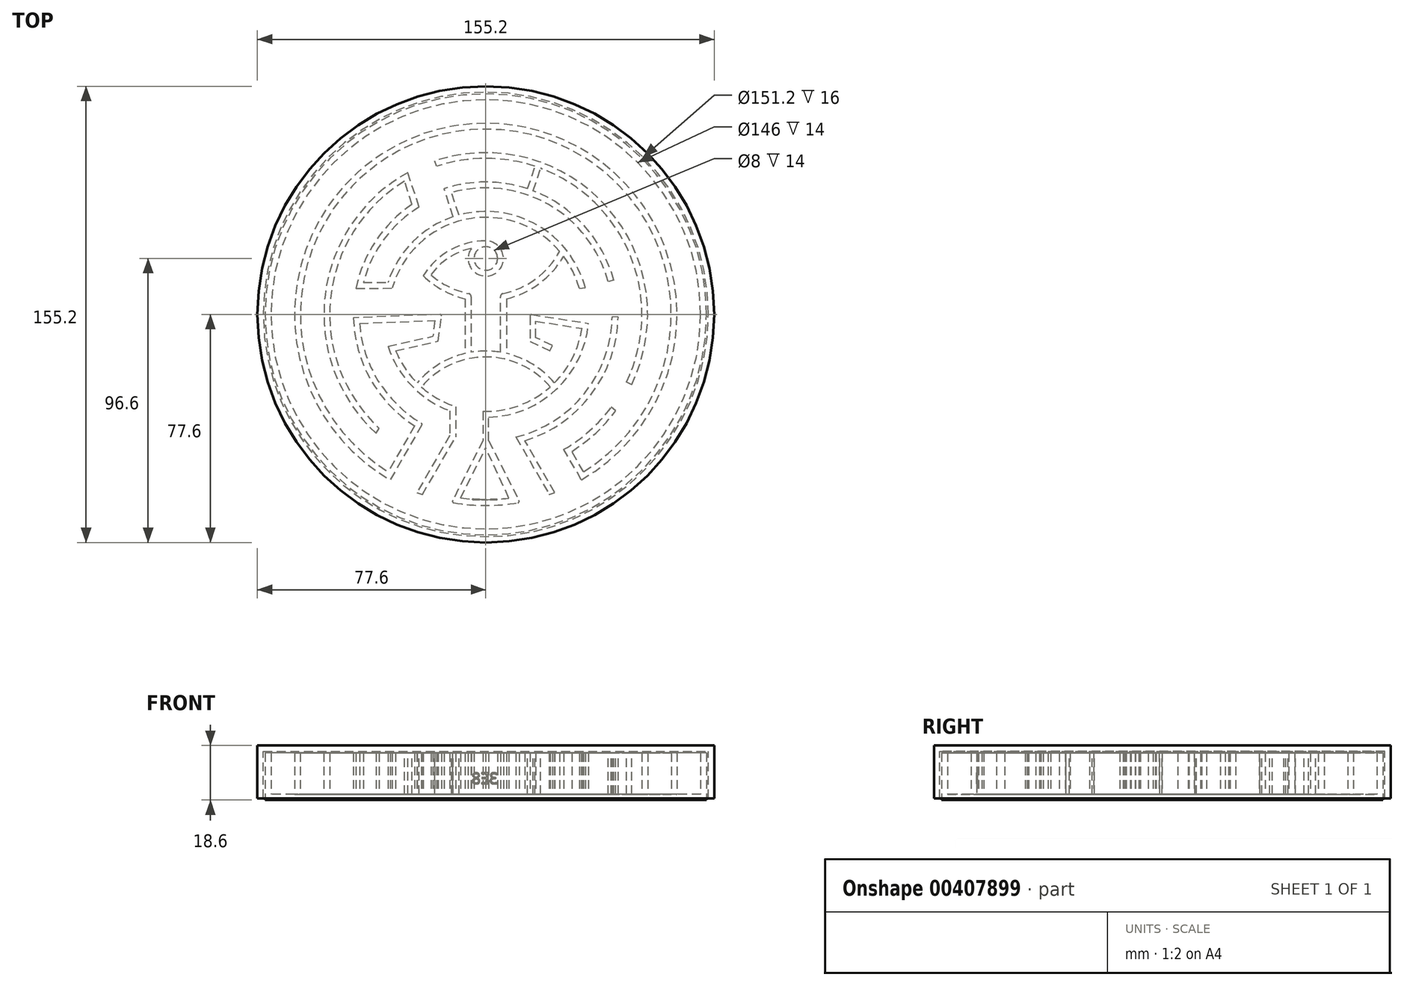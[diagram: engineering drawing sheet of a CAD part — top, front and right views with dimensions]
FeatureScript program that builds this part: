
annotation { "Feature Type Name" : "Feature", "Feature Type Description" : "" }
export const myFeature = defineFeature(function(context is Context, id is Id, definition is map)
    precondition{}
    {
        {
            assignVariable(context, id + "F0", {"name" : "OuterDiam", "anyValue" : 150});
        }
        {
            assignVariable(context, id + "F1", {"name" : "ChannelWidth", "anyValue" : getVariable(context, 'OuterDiam') / 15});
        }
        {
            assignVariable(context, id + "F2", {"name" : "WallThick", "anyValue" : 2});
        }
        {
            assignVariable(context, id + "F3", {"name" : "WallHeight", "anyValue" : getVariable(context, 'ChannelWidth') + getVariable(context, 'WallThick') * 2});
        }
        {
            var Q0;
            Q0=qCreatedBy(makeId("Top.planeOp"),FACE);
            var sketch = newSketch(context, id + "F4", { "sketchPlane" : qUnion([Q0])});
            skCircle(sketch, "E0", {"center": v(0, 0) * mm, "radius": 75 * mm});
            skSolve(sketch);
        }
        {
            var Q0;
            Q0=makeQuery(id+"F4.imprint","IMPRINT",FACE,{"disambiguationData":[TD([[makeQuery(id+"F4.imprint","IMPRINT",EDGE,{"derivedFrom":sQuery(id+"F4.wireOp",EDGE,"E0")}),1.0]])]});
            extrude(context, id + "F5", {"entities" : qUnion([Q0]), "depth" : (getVariable(context, 'WallThick')) * mm});
        }
        {
            var Q0;
            Q0=makeQuery(id+"F5.opExtrude","CAP_FACE",FACE,{"disambiguationData":[OSD([sQuery(id+"F4.wireOp",EDGE,"E0")])],"isStart":false});
            var sketch = newSketch(context, id + "F6", { "sketchPlane" : qUnion([Q0])});
            skCircle(sketch, "E1.0", {"center": v(0, 0) * mm, "radius": 75 * mm});
            skCircle(sketch, "E2.0", {"center": v(0, 0) * mm, "radius": 73 * mm});
            skCircle(sketch, "E3", {"center": v(0, 0) * mm, "radius": 65 * mm, "construction": true});
            skCircle(sketch, "E4", {"center": v(0, 0) * mm, "radius": 55 * mm, "construction": true});
            skCircle(sketch, "E5", {"center": v(0, 0) * mm, "radius": 45 * mm, "construction": true});
            skCircle(sketch, "E6", {"center": v(0, 0) * mm, "radius": 35 * mm, "construction": true});
            skCircle(sketch, "E7", {"center": v(0, 0) * mm, "radius": 5 * mm, "construction": true});
            skLineSegment(sketch, "E8", {"start": v(0, 35) * mm, "end": v(0, 45) * mm, "construction": true});
            skLineSegment(sketch, "E9", {"start": v(0, 45) * mm, "end": v(0, 55) * mm, "construction": true});
            skLineSegment(sketch, "E10", {"start": v(0, 55) * mm, "end": v(0, 65) * mm, "construction": true});
            skLineSegment(sketch, "E11", {"start": v(0, 65) * mm, "end": v(0, 75) * mm, "construction": true});
            skLineSegment(sketch, "E12", {"start": v(0, 0) * mm, "end": v(24.75, 24.75) * mm, "construction": true});
            skLineSegment(sketch, "E13", {"start": v(0, 0) * mm, "end": v(75, 0) * mm, "construction": true});
            skLineSegment(sketch, "E14.MirrorCS", {"start": v(0, 0) * mm, "end": v(24.75, -24.75) * mm, "construction": true});
            skLineSegment(sketch, "E15.MirrorCS", {"start": v(0, 0) * mm, "end": v(-16.5, 16.5) * mm, "construction": true});
            skLineSegment(sketch, "E16.MirrorCS", {"start": v(0, 0) * mm, "end": v(-23.33, -23.33) * mm, "construction": true});
            skCircle(sketch, "E17", {"center": v(0, 0) * mm, "radius": 10 * mm, "construction": true});
            skArc(sketch, "E18", {"start": v(-21.28, 13.13) * mm, "mid": v(-14.67, 8.24) * mm, "end": v(-7, 5.3) * mm});
            skArc(sketch, "E19", {"start": v(-18.67, 13.44) * mm, "mid": v(-12.27, 9.26) * mm, "end": v(-5, 6.92) * mm});
            skLineSegment(sketch, "E20", {"start": v(-7, 5.3) * mm, "end": v(-7, -13.3) * mm});
            skLineSegment(sketch, "E21", {"start": v(-5, 6.92) * mm, "end": v(-5, -12.9) * mm});
            skCircle(sketch, "E22.MirrorC", {"center": v(0, -43) * mm, "radius": 28.52 * mm, "construction": true});
            skArc(sketch, "E23", {"start": v(41.14, -50.32) * mm, "mid": v(-5.25, 64.79) * mm, "end": v(-32.5, -56.3) * mm});
            skArc(sketch, "E24", {"start": v(32.5, -56.3) * mm, "mid": v(0, 65) * mm, "end": v(-32.5, -56.3) * mm});
            skLineSegment(sketch, "E25", {"start": v(15.1, -7.04) * mm, "end": v(0, 0) * mm, "construction": true});
            skArc(sketch, "E26", {"start": v(-30.61, -12.33) * mm, "mid": v(-27.53, -18.2) * mm, "end": v(-23.33, -23.33) * mm});
            skArc(sketch, "E27", {"start": v(-7, -13.3) * mm, "mid": v(-15.98, -17) * mm, "end": v(-23.33, -23.33) * mm});
            skArc(sketch, "E28", {"start": v(-33.27, -10.87) * mm, "mid": v(-25.26, -24.22) * mm, "end": v(-12.25, -32.79) * mm});
            skLineSegment(sketch, "E29", {"start": v(-33.27, -10.87) * mm, "end": v(-17.96, -7.48) * mm});
            skArc(sketch, "E30", {"start": v(5, -12.9) * mm, "mid": v(0, -12.48) * mm, "end": v(-5, -12.9) * mm});
            skLineSegment(sketch, "E31", {"start": v(5, -12.9) * mm, "end": v(5, 6.92) * mm});
            skLineSegment(sketch, "E32", {"start": v(7, 5.3) * mm, "end": v(7, -13.3) * mm});
            skArc(sketch, "E33", {"start": v(5, 6.92) * mm, "mid": v(16.7, 11.88) * mm, "end": v(25.09, 21.44) * mm});
            skArc(sketch, "E34", {"start": v(33.22, -53.53) * mm, "mid": v(0, 63) * mm, "end": v(-33.22, -53.53) * mm});
            skArc(sketch, "E35", {"start": v(-44.99, -1.15) * mm, "mid": v(-39.18, -22.13) * mm, "end": v(-24.2, -37.93) * mm});
            skArc(sketch, "E36", {"start": v(-21.88, -24.7) * mm, "mid": v(-16.4, -28.63) * mm, "end": v(-10.25, -31.37) * mm});
            skArc(sketch, "E37", {"start": v(-42.9, -3.07) * mm, "mid": v(-36.45, -22.82) * mm, "end": v(-21.5, -37.24) * mm});
            skLineSegment(sketch, "E38", {"start": v(-17.28, -2.09) * mm, "end": v(-17.96, -7.48) * mm});
            skLineSegment(sketch, "E39", {"start": v(-30.61, -12.33) * mm, "end": v(-16.15, -9.13) * mm});
            skLineSegment(sketch, "E40", {"start": v(-16.15, -9.13) * mm, "end": v(-15, 0) * mm});
            skLineSegment(sketch, "E41", {"start": v(-10.25, -31.37) * mm, "end": v(-10.25, -41.76) * mm});
            skLineSegment(sketch, "E42", {"start": v(-12.25, -32.79) * mm, "end": v(-12.25, -41.22) * mm});
            skLineSegment(sketch, "E43", {"start": v(0, -43) * mm, "end": v(0, -45) * mm, "construction": true});
            skLineSegment(sketch, "E44", {"start": v(-1, -32.98) * mm, "end": v(-1, -42.99) * mm});
            skArc(sketch, "E45", {"start": v(-1, -32.98) * mm, "mid": v(11.23, -31.03) * mm, "end": v(21.88, -24.7) * mm});
            skLineSegment(sketch, "E46", {"start": v(1, -42.99) * mm, "end": v(1, -34.99) * mm});
            skLineSegment(sketch, "E47", {"start": v(15, 0) * mm, "end": v(15, -9.2) * mm});
            skLineSegment(sketch, "E48", {"start": v(21.81, -12.38) * mm, "end": v(22.66, -10.57) * mm});
            skLineSegment(sketch, "E49", {"start": v(22.66, -10.57) * mm, "end": v(17, -7.93) * mm});
            skLineSegment(sketch, "E50", {"start": v(17, -7.93) * mm, "end": v(17, -2.33) * mm});
            skArc(sketch, "E51", {"start": v(23.33, -23.33) * mm, "mid": v(15.98, -17) * mm, "end": v(7, -13.3) * mm});
            skArc(sketch, "E52", {"start": v(21.88, -24.7) * mm, "mid": v(0, -14.48) * mm, "end": v(-21.88, -24.7) * mm});
            skLineSegment(sketch, "E53", {"start": v(15, -9.2) * mm, "end": v(21.81, -12.38) * mm});
            skLineSegment(sketch, "E54", {"start": v(15, 0) * mm, "end": v(34.86, -3.07) * mm});
            skLineSegment(sketch, "E55", {"start": v(17, -2.33) * mm, "end": v(32.66, -4.75) * mm});
            skArc(sketch, "E56", {"start": v(23.33, -23.33) * mm, "mid": v(29.5, -14.8) * mm, "end": v(32.66, -4.75) * mm});
            skArc(sketch, "E57", {"start": v(1, -34.99) * mm, "mid": v(24, -25.47) * mm, "end": v(34.86, -3.07) * mm});
            skArc(sketch, "E58", {"start": v(31.8, 8.81) * mm, "mid": v(0.05, 33) * mm, "end": v(-31.77, 8.91) * mm});
            skArc(sketch, "E59", {"start": v(33.8, 9.07) * mm, "mid": v(0.96, 34.99) * mm, "end": v(-33.26, 10.9) * mm});
            skLineSegment(sketch, "E60", {"start": v(31.8, 8.81) * mm, "end": v(33.8, 9.07) * mm});
            skLineSegment(sketch, "E61", {"start": v(-32.5, -56.3) * mm, "end": v(0, 0) * mm, "construction": true});
            skLineSegment(sketch, "E62", {"start": v(-21.5, -37.24) * mm, "end": v(-32.5, -56.3) * mm});
            skLineSegment(sketch, "E63", {"start": v(-24.2, -37.93) * mm, "end": v(-33.22, -53.53) * mm});
            skArc(sketch, "E64", {"start": v(29.21, -46.6) * mm, "mid": v(5.04, 54.77) * mm, "end": v(-37.23, -40.48) * mm});
            skArc(sketch, "E65", {"start": v(26.52, -45.94) * mm, "mid": v(6.04, 52.7) * mm, "end": v(-36.23, -38.75) * mm});
            skLineSegment(sketch, "E66", {"start": v(-37.23, -40.48) * mm, "end": v(-36.23, -38.75) * mm});
            skLineSegment(sketch, "E67", {"start": v(0, 0) * mm, "end": v(32.5, -56.3) * mm, "construction": true});
            skLineSegment(sketch, "E68", {"start": v(32.5, -56.3) * mm, "end": v(26.52, -45.94) * mm});
            skLineSegment(sketch, "E69", {"start": v(33.22, -53.53) * mm, "end": v(29.21, -46.6) * mm});
            skLineSegment(sketch, "E70", {"start": v(-12.25, -41.22) * mm, "end": v(-23.45, -60.62) * mm});
            skLineSegment(sketch, "E71", {"start": v(-23.45, -60.62) * mm, "end": v(-21.58, -61.31) * mm});
            skLineSegment(sketch, "E72", {"start": v(-21.58, -61.31) * mm, "end": v(-10.25, -41.76) * mm});
            skLineSegment(sketch, "E73", {"start": v(-1, -42.99) * mm, "end": v(-11.58, -63.96) * mm});
            skArc(sketch, "E74", {"start": v(13.28, -43) * mm, "mid": v(30.17, 33.4) * mm, "end": v(-44.12, 8.85) * mm});
            skArc(sketch, "E75", {"start": v(10.28, -41.75) * mm, "mid": v(30.62, 30.2) * mm, "end": v(-41.6, 10.87) * mm});
            skLineSegment(sketch, "E76", {"start": v(-41.6, 10.87) * mm, "end": v(-33.26, 10.9) * mm});
            skLineSegment(sketch, "E77", {"start": v(-44.12, 8.85) * mm, "end": v(-31.77, 8.91) * mm});
            skLineSegment(sketch, "E78", {"start": v(10.28, -41.75) * mm, "end": v(21.58, -61.31) * mm});
            skLineSegment(sketch, "E79", {"start": v(21.58, -61.31) * mm, "end": v(23.45, -60.62) * mm});
            skLineSegment(sketch, "E80", {"start": v(23.45, -60.62) * mm, "end": v(13.28, -43) * mm});
            skArc(sketch, "E81", {"start": v(-21.5, -37.24) * mm, "mid": v(-6.05, -42.57) * mm, "end": v(10.28, -41.75) * mm, "construction": true});
            skLineSegment(sketch, "E82", {"start": v(1, -42.99) * mm, "end": v(11.58, -63.96) * mm});
            skArc(sketch, "E83", {"start": v(-11.58, -63.96) * mm, "mid": v(0, -65) * mm, "end": v(11.58, -63.96) * mm});
            skArc(sketch, "E84", {"start": v(-8.56, -62.42) * mm, "mid": v(-0.35, -63) * mm, "end": v(7.87, -62.5) * mm});
            skLineSegment(sketch, "E85", {"start": v(-8.56, -62.42) * mm, "end": v(0, -45.45) * mm});
            skLineSegment(sketch, "E86", {"start": v(7.87, -62.5) * mm, "end": v(0, -45.45) * mm});
            skLineSegment(sketch, "E87", {"start": v(0, 5) * mm, "end": v(0, 15) * mm, "construction": true});
            skLineSegment(sketch, "E88", {"start": v(0, 15) * mm, "end": v(0, 25) * mm, "construction": true});
            skLineSegment(sketch, "E89", {"start": v(0, 25) * mm, "end": v(0, 35) * mm, "construction": true});
            skCircle(sketch, "E90", {"center": v(0, 0) * mm, "radius": 25 * mm, "construction": true});
            skArc(sketch, "E91", {"start": v(0, 25) * mm, "mid": v(-12.18, 21.83) * mm, "end": v(-21.28, 13.13) * mm});
            skArc(sketch, "E92", {"start": v(-4.9, 22.47) * mm, "mid": v(-12.62, 19.23) * mm, "end": v(-18.67, 13.44) * mm});
            skArc(sketch, "E93", {"start": v(-4.9, 22.47) * mm, "mid": v(2.75, 13.67) * mm, "end": v(0, 25) * mm});
            skCircle(sketch, "E94", {"center": v(0, 19) * mm, "radius": 4 * mm});
            skLineSegment(sketch, "E95", {"start": v(4, 19) * mm, "end": v(6, 19) * mm, "construction": true});
            skLineSegment(sketch, "E96", {"start": v(5, 19) * mm, "end": v(5, 6.92) * mm, "construction": true});
            skArc(sketch, "E97", {"start": v(7, 5.3) * mm, "mid": v(18.21, 10.51) * mm, "end": v(26.43, 19.75) * mm});
            skLineSegment(sketch, "E98", {"start": v(-42.9, -3.07) * mm, "end": v(-17.28, -2.09) * mm});
            skLineSegment(sketch, "E99", {"start": v(-15, 0) * mm, "end": v(-44.99, -1.15) * mm});
            skLineSegment(sketch, "E100", {"start": v(-15, 0) * mm, "end": v(15, 0) * mm, "construction": true});
            skLineSegment(sketch, "E101", {"start": v(0, 5) * mm, "end": v(0, 0) * mm, "construction": true});
            skSolve(sketch);
        }
        {
            var Q0;
            Q0=makeQuery(id+"F6.imprint","IMPRINT",FACE,{"disambiguationData":[TD([[makeQuery(id+"F6.imprint","IMPRINT",EDGE,{"derivedFrom":sQuery(id+"F6.wireOp",EDGE,"E1.0")}),1.0]])]});
            var Q1;
            Q1=makeQuery(id+"F6.imprint","IMPRINT",FACE,{"disambiguationData":[TD([[makeQuery(id+"F6.imprint","IMPRINT",EDGE,{"derivedFrom":sQuery(id+"F6.wireOp",EDGE,"E18")}),1.0]])]});
            var Q2;
            Q2=makeQuery(id+"F6.imprint","IMPRINT",FACE,{"disambiguationData":[TD([[makeQuery(id+"F6.imprint","IMPRINT",EDGE,{"derivedFrom":sQuery(id+"F6.wireOp",EDGE,"E59")}),1.0]])]});
            extrude(context, id + "F7", {"entities" : qUnion([Q0, Q1, Q2]), "operationType" : NewBodyOperationType.ADD, "depth" : (getVariable(context, 'WallHeight')) * mm});
        }
        {
            var Q0;
            Q0=makeQuery(id+"F7.opExtrude","CAP_FACE",FACE,{"disambiguationData":[OSD([sQuery(id+"F6.wireOp",EDGE,"TA0vL4iM-hI7p-0iIZ-EZH9-pWyA7mMgioLP"),sQuery(id+"F6.wireOp",EDGE,"eVbhxhPi-amxz-cSnw-BDjh-pJRtyq95g7uy"),sQuery(id+"F6.wireOp",EDGE,"3bY1lwaK-FQGh-TaTl-XcqF-0j4MG99JuUr8"),sQuery(id+"F6.wireOp",EDGE,"r5nHWF7N-89Eq-ztux-vKRJ-OAizSOWOkK4G"),sQuery(id+"F6.wireOp",EDGE,"vSMcaTa0-RPhz-RhFH-5GNV-4O4aKqDjyfSq"),sQuery(id+"F6.wireOp",EDGE,"E18"),sQuery(id+"F6.wireOp",EDGE,"E19"),sQuery(id+"F6.wireOp",EDGE,"c2zhrxeP-xiZB-5hTI-5geB-tCFFj0RtpMOh"),sQuery(id+"F6.wireOp",EDGE,"E20"),sQuery(id+"F6.wireOp",EDGE,"E21"),sQuery(id+"F6.wireOp",EDGE,"E24"),sQuery(id+"F6.wireOp",EDGE,"E26"),sQuery(id+"F6.wireOp",EDGE,"E27"),sQuery(id+"F6.wireOp",EDGE,"E28"),sQuery(id+"F6.wireOp",EDGE,"E29"),sQuery(id+"F6.wireOp",EDGE,"E30"),sQuery(id+"F6.wireOp",EDGE,"E31"),sQuery(id+"F6.wireOp",EDGE,"E32"),sQuery(id+"F6.wireOp",EDGE,"E33"),sQuery(id+"F6.wireOp",EDGE,"w3oIxx7T-loaL-NBMZ-wnJf-bmkmqDUJZ4SM"),sQuery(id+"F6.wireOp",EDGE,"E34"),sQuery(id+"F6.wireOp",EDGE,"E35"),sQuery(id+"F6.wireOp",EDGE,"QwFV82SE-m3OC-BQkn-0jzC-JCZTuH3WHQPn"),sQuery(id+"F6.wireOp",EDGE,"E36"),sQuery(id+"F6.wireOp",EDGE,"E37"),sQuery(id+"F6.wireOp",EDGE,"ANerLEZW-9gPT-yuOP-Ji07-4zPnV21XRaUt"),sQuery(id+"F6.wireOp",EDGE,"E38"),sQuery(id+"F6.wireOp",EDGE,"E39"),sQuery(id+"F6.wireOp",EDGE,"E40"),sQuery(id+"F6.wireOp",EDGE,"E41"),sQuery(id+"F6.wireOp",EDGE,"E42"),sQuery(id+"F6.wireOp",EDGE,"E44"),sQuery(id+"F6.wireOp",EDGE,"E45"),sQuery(id+"F6.wireOp",EDGE,"E46"),sQuery(id+"F6.wireOp",EDGE,"E47"),sQuery(id+"F6.wireOp",EDGE,"E48"),sQuery(id+"F6.wireOp",EDGE,"E49"),sQuery(id+"F6.wireOp",EDGE,"E50"),sQuery(id+"F6.wireOp",EDGE,"E51"),sQuery(id+"F6.wireOp",EDGE,"E52"),sQuery(id+"F6.wireOp",EDGE,"E53"),sQuery(id+"F6.wireOp",EDGE,"E54"),sQuery(id+"F6.wireOp",EDGE,"E55"),sQuery(id+"F6.wireOp",EDGE,"E56"),sQuery(id+"F6.wireOp",EDGE,"E57"),sQuery(id+"F6.wireOp",EDGE,"E58"),sQuery(id+"F6.wireOp",EDGE,"E59"),sQuery(id+"F6.wireOp",EDGE,"E60"),sQuery(id+"F6.wireOp",EDGE,"E62"),sQuery(id+"F6.wireOp",EDGE,"E63"),sQuery(id+"F6.wireOp",EDGE,"E64"),sQuery(id+"F6.wireOp",EDGE,"E65"),sQuery(id+"F6.wireOp",EDGE,"E66"),sQuery(id+"F6.wireOp",EDGE,"E68"),sQuery(id+"F6.wireOp",EDGE,"E69"),sQuery(id+"F6.wireOp",EDGE,"E70"),sQuery(id+"F6.wireOp",EDGE,"E71"),sQuery(id+"F6.wireOp",EDGE,"E72"),sQuery(id+"F6.wireOp",EDGE,"E73"),sQuery(id+"F6.wireOp",EDGE,"E74"),sQuery(id+"F6.wireOp",EDGE,"E75"),sQuery(id+"F6.wireOp",EDGE,"E76"),sQuery(id+"F6.wireOp",EDGE,"E77"),sQuery(id+"F6.wireOp",EDGE,"E78"),sQuery(id+"F6.wireOp",EDGE,"E79"),sQuery(id+"F6.wireOp",EDGE,"E80"),sQuery(id+"F6.wireOp",EDGE,"E82"),sQuery(id+"F6.wireOp",EDGE,"E83"),sQuery(id+"F6.wireOp",EDGE,"E84"),sQuery(id+"F6.wireOp",EDGE,"E85"),sQuery(id+"F6.wireOp",EDGE,"E86")])],"isStart":false});
            var sketch = newSketch(context, id + "F8", { "sketchPlane" : qUnion([Q0])});
            skPoint(sketch, "E102.0", {"position": v(0, 0) * mm});
            skPoint(sketch, "E103.0", {"position": v(33.8, 9.07) * mm});
            skLineSegment(sketch, "E104", {"start": v(0, 0) * mm, "end": v(43.46, 11.66) * mm, "construction": true});
            skArc(sketch, "E105", {"start": v(45, -0.9) * mm, "mid": v(44.67, 5.43) * mm, "end": v(43.46, 11.66) * mm});
            skArc(sketch, "E106", {"start": v(43, -0.86) * mm, "mid": v(42.69, 5.2) * mm, "end": v(41.53, 11.14) * mm});
            skLineSegment(sketch, "E107", {"start": v(0, 0) * mm, "end": v(45, -0.9) * mm, "construction": true});
            skLineSegment(sketch, "E108", {"start": v(43, -0.86) * mm, "end": v(45, -0.9) * mm});
            skLineSegment(sketch, "E109", {"start": v(41.53, 11.14) * mm, "end": v(43.46, 11.66) * mm});
            skLineSegment(sketch, "E110", {"start": v(0, 0) * mm, "end": v(49.54, -23.88) * mm, "construction": true});
            skLineSegment(sketch, "E111", {"start": v(0, 0) * mm, "end": v(44.18, -32.76) * mm, "construction": true});
            skArc(sketch, "E112", {"start": v(42.61, -31.6) * mm, "mid": v(45.4, -27.44) * mm, "end": v(47.79, -23.04) * mm});
            skArc(sketch, "E113", {"start": v(44.18, -32.76) * mm, "mid": v(47.07, -28.45) * mm, "end": v(49.54, -23.88) * mm});
            skLineSegment(sketch, "E114", {"start": v(47.79, -23.04) * mm, "end": v(49.54, -23.88) * mm});
            skLineSegment(sketch, "E115", {"start": v(42.61, -31.6) * mm, "end": v(44.18, -32.76) * mm});
            skLineSegment(sketch, "E116", {"start": v(0, 0) * mm, "end": v(45.4, -27.44) * mm, "construction": true});
            skLineSegment(sketch, "E117", {"start": v(0, 0) * mm, "end": v(-17.37, 52.19) * mm, "construction": true});
            skArc(sketch, "E118", {"start": v(-17.37, 52.19) * mm, "mid": v(-22.03, 50.4) * mm, "end": v(-26.5, 48.2) * mm});
            skArc(sketch, "E119", {"start": v(-13.58, 40.8) * mm, "mid": v(-18.23, 38.94) * mm, "end": v(-22.64, 36.56) * mm});
            skLineSegment(sketch, "E120", {"start": v(-26.5, 48.2) * mm, "end": v(-22.64, 36.56) * mm});
            skLineSegment(sketch, "E121", {"start": v(-17.37, 52.19) * mm, "end": v(-13.58, 40.8) * mm});
            skSolve(sketch);
        }
        {
            var Q0;
            Q0 = qSketchRegion(id + "F8", true);
            var Q1;
            Q1=makeQuery(id+"F7.boolean.opBoolean","SPLIT",FACE,{"disambiguationData":[TD([makeQuery(id+"F7.opExtrude","SWEPT_FACE",FACE,{"disambiguationData":[OSD([sQuery(id+"F6.wireOp",EDGE,"E2.0")])]})])],"derivedFrom":makeQuery(id+"F5.opExtrude","CAP_FACE",FACE,{"disambiguationData":[OSD([sQuery(id+"F4.wireOp",EDGE,"E0")])],"isStart":false})});
            extrude(context, id + "F9", {"entities" : qUnion([Q0]), "operationType" : NewBodyOperationType.REMOVE, "endBound" : BoundingType.UP_TO_SURFACE, "oppositeDirection" : true, "endBoundEntityFace" : qUnion([Q1]), "depth" : 25 * mm});
        }
        {
            var Q0;
            {var subQ0=sQuery(id+"F6.wireOp",EDGE,"E64");var subQ1=sQuery(id+"F6.wireOp",EDGE,"E65");Q0=makeQuery(id+"F9.boolean.opBoolean","SPLIT",FACE,{"disambiguationData":[TD([makeQuery(id+"F9.opExtrude","SWEPT_FACE",FACE,{"disambiguationData":[OSD([sQuery(id+"F8.wireOp",EDGE,"E114")])]})])],"derivedFrom":makeQuery(id+"F7.opExtrude","CAP_FACE",FACE,{"disambiguationData":[OSD([sQuery(id+"F6.wireOp",EDGE,"TA0vL4iM-hI7p-0iIZ-EZH9-pWyA7mMgioLP"),sQuery(id+"F6.wireOp",EDGE,"eVbhxhPi-amxz-cSnw-BDjh-pJRtyq95g7uy"),sQuery(id+"F6.wireOp",EDGE,"3bY1lwaK-FQGh-TaTl-XcqF-0j4MG99JuUr8"),sQuery(id+"F6.wireOp",EDGE,"r5nHWF7N-89Eq-ztux-vKRJ-OAizSOWOkK4G"),sQuery(id+"F6.wireOp",EDGE,"vSMcaTa0-RPhz-RhFH-5GNV-4O4aKqDjyfSq"),sQuery(id+"F6.wireOp",EDGE,"E18"),sQuery(id+"F6.wireOp",EDGE,"E19"),sQuery(id+"F6.wireOp",EDGE,"c2zhrxeP-xiZB-5hTI-5geB-tCFFj0RtpMOh"),sQuery(id+"F6.wireOp",EDGE,"E20"),sQuery(id+"F6.wireOp",EDGE,"E21"),sQuery(id+"F6.wireOp",EDGE,"E24"),sQuery(id+"F6.wireOp",EDGE,"E26"),sQuery(id+"F6.wireOp",EDGE,"E27"),sQuery(id+"F6.wireOp",EDGE,"E28"),sQuery(id+"F6.wireOp",EDGE,"E29"),sQuery(id+"F6.wireOp",EDGE,"E30"),sQuery(id+"F6.wireOp",EDGE,"E31"),sQuery(id+"F6.wireOp",EDGE,"E32"),sQuery(id+"F6.wireOp",EDGE,"E33"),sQuery(id+"F6.wireOp",EDGE,"w3oIxx7T-loaL-NBMZ-wnJf-bmkmqDUJZ4SM"),sQuery(id+"F6.wireOp",EDGE,"E34"),sQuery(id+"F6.wireOp",EDGE,"E35"),sQuery(id+"F6.wireOp",EDGE,"QwFV82SE-m3OC-BQkn-0jzC-JCZTuH3WHQPn"),sQuery(id+"F6.wireOp",EDGE,"E36"),sQuery(id+"F6.wireOp",EDGE,"E37"),sQuery(id+"F6.wireOp",EDGE,"ANerLEZW-9gPT-yuOP-Ji07-4zPnV21XRaUt"),sQuery(id+"F6.wireOp",EDGE,"E38"),sQuery(id+"F6.wireOp",EDGE,"E39"),sQuery(id+"F6.wireOp",EDGE,"E40"),sQuery(id+"F6.wireOp",EDGE,"E41"),sQuery(id+"F6.wireOp",EDGE,"E42"),sQuery(id+"F6.wireOp",EDGE,"E44"),sQuery(id+"F6.wireOp",EDGE,"E45"),sQuery(id+"F6.wireOp",EDGE,"E46"),sQuery(id+"F6.wireOp",EDGE,"E47"),sQuery(id+"F6.wireOp",EDGE,"E48"),sQuery(id+"F6.wireOp",EDGE,"E49"),sQuery(id+"F6.wireOp",EDGE,"E50"),sQuery(id+"F6.wireOp",EDGE,"E51"),sQuery(id+"F6.wireOp",EDGE,"E52"),sQuery(id+"F6.wireOp",EDGE,"E53"),sQuery(id+"F6.wireOp",EDGE,"E54"),sQuery(id+"F6.wireOp",EDGE,"E55"),sQuery(id+"F6.wireOp",EDGE,"E56"),sQuery(id+"F6.wireOp",EDGE,"E57"),sQuery(id+"F6.wireOp",EDGE,"E58"),sQuery(id+"F6.wireOp",EDGE,"E59"),sQuery(id+"F6.wireOp",EDGE,"E60"),sQuery(id+"F6.wireOp",EDGE,"E62"),sQuery(id+"F6.wireOp",EDGE,"E63"),subQ0,subQ1,sQuery(id+"F6.wireOp",EDGE,"E66"),sQuery(id+"F6.wireOp",EDGE,"E68"),sQuery(id+"F6.wireOp",EDGE,"E69"),sQuery(id+"F6.wireOp",EDGE,"E70"),sQuery(id+"F6.wireOp",EDGE,"E71"),sQuery(id+"F6.wireOp",EDGE,"E72"),sQuery(id+"F6.wireOp",EDGE,"E73"),sQuery(id+"F6.wireOp",EDGE,"E74"),sQuery(id+"F6.wireOp",EDGE,"E75"),sQuery(id+"F6.wireOp",EDGE,"E76"),sQuery(id+"F6.wireOp",EDGE,"E77"),sQuery(id+"F6.wireOp",EDGE,"E78"),sQuery(id+"F6.wireOp",EDGE,"E79"),sQuery(id+"F6.wireOp",EDGE,"E80"),sQuery(id+"F6.wireOp",EDGE,"E82"),sQuery(id+"F6.wireOp",EDGE,"E83"),sQuery(id+"F6.wireOp",EDGE,"E84"),sQuery(id+"F6.wireOp",EDGE,"E85"),sQuery(id+"F6.wireOp",EDGE,"E86")])],"isStart":false})});}
            var sketch = newSketch(context, id + "F10", { "sketchPlane" : qUnion([Q0])});
            skArc(sketch, "E122.0", {"start": v(43.46, 11.66) * mm, "mid": v(21.33, 39.63) * mm, "end": v(-14.21, 42.7) * mm, "construction": true});
            skArc(sketch, "E123.0", {"start": v(47.79, -23.04) * mm, "mid": v(39.83, 35.04) * mm, "end": v(-16.75, 50.34) * mm, "construction": true});
            skArc(sketch, "E124.0", {"start": v(-25.88, 46.3) * mm, "mid": v(-52.66, 6.4) * mm, "end": v(-36.23, -38.75) * mm, "construction": true});
            skLineSegment(sketch, "E125", {"start": v(-25.88, 46.3) * mm, "end": v(-23.28, 38.5) * mm});
            skLineSegment(sketch, "E126", {"start": v(-27.64, 45.28) * mm, "end": v(-25.02, 37.4) * mm});
            skArc(sketch, "E127", {"start": v(-25.88, 46.3) * mm, "mid": v(-26.77, 45.8) * mm, "end": v(-27.64, 45.28) * mm});
            skArc(sketch, "E128", {"start": v(-23.28, 38.5) * mm, "mid": v(-24.16, 37.96) * mm, "end": v(-25.02, 37.4) * mm});
            skArc(sketch, "E129.0", {"start": v(41.53, 11.14) * mm, "mid": v(20.38, 37.86) * mm, "end": v(-13.58, 40.8) * mm});
            skLineSegment(sketch, "E130", {"start": v(-13.58, 40.8) * mm, "end": v(-11.05, 33.2) * mm});
            skLineSegment(sketch, "E131", {"start": v(-11.67, 41.39) * mm, "end": v(-9.14, 33.79) * mm});
            skArc(sketch, "E132", {"start": v(-11.67, 41.39) * mm, "mid": v(-12.63, 41.1) * mm, "end": v(-13.58, 40.8) * mm});
            skArc(sketch, "E133", {"start": v(-9.14, 33.79) * mm, "mid": v(-10.1, 33.51) * mm, "end": v(-11.05, 33.2) * mm});
            skLineSegment(sketch, "E134", {"start": v(0, 0) * mm, "end": v(16.75, 50.34) * mm, "construction": true});
            skLineSegment(sketch, "E135", {"start": v(16.75, 50.34) * mm, "end": v(14.21, 42.7) * mm});
            skLineSegment(sketch, "E136", {"start": v(18.64, 49.67) * mm, "end": v(16.1, 42.02) * mm});
            skArc(sketch, "E137", {"start": v(16.1, 42.02) * mm, "mid": v(15.16, 42.37) * mm, "end": v(14.21, 42.7) * mm});
            skArc(sketch, "E138", {"start": v(18.64, 49.67) * mm, "mid": v(17.7, 50.01) * mm, "end": v(16.75, 50.34) * mm});
            skArc(sketch, "E139.0", {"start": v(33.8, 9.07) * mm, "mid": v(0.96, 34.99) * mm, "end": v(-33.26, 10.9) * mm, "construction": true});
            skArc(sketch, "E140.0", {"start": v(-23.28, 38.5) * mm, "mid": v(-36.82, 25.87) * mm, "end": v(-44.12, 8.85) * mm, "construction": true});
            skSolve(sketch);
        }
        {
            var Q0;
            Q0 = qSketchRegion(id + "F10", true);
            var Q1;
            Q1=makeQuery(id+"F9.boolean.opBoolean","MERGE",FACE,{"derivedFrom":[makeQuery(id+"F7.boolean.opBoolean","SPLIT",FACE,{"disambiguationData":[TD([makeQuery(id+"F7.opExtrude","SWEPT_FACE",FACE,{"disambiguationData":[OSD([sQuery(id+"F6.wireOp",EDGE,"E2.0")])]})])],"derivedFrom":makeQuery(id+"F5.opExtrude","CAP_FACE",FACE,{"disambiguationData":[OSD([sQuery(id+"F4.wireOp",EDGE,"E0")])],"isStart":false})}),makeQuery(id+"F9.opExtrude","CAP_FACE",FACE,{"disambiguationData":[OSD([sQuery(id+"F8.wireOp",EDGE,"E105"),sQuery(id+"F8.wireOp",EDGE,"E106"),sQuery(id+"F8.wireOp",EDGE,"E108"),sQuery(id+"F8.wireOp",EDGE,"E109")])],"isStart":false}),makeQuery(id+"F9.opExtrude","CAP_FACE",FACE,{"disambiguationData":[OSD([sQuery(id+"F8.wireOp",EDGE,"E112"),sQuery(id+"F8.wireOp",EDGE,"E113"),sQuery(id+"F8.wireOp",EDGE,"E114"),sQuery(id+"F8.wireOp",EDGE,"E115")])],"isStart":false}),makeQuery(id+"F9.opExtrude","CAP_FACE",FACE,{"disambiguationData":[OSD([sQuery(id+"F8.wireOp",EDGE,"E118"),sQuery(id+"F8.wireOp",EDGE,"E119"),sQuery(id+"F8.wireOp",EDGE,"E120"),sQuery(id+"F8.wireOp",EDGE,"E121")])],"isStart":false})]});
            extrude(context, id + "F11", {"entities" : qUnion([Q0]), "operationType" : NewBodyOperationType.ADD, "endBound" : BoundingType.UP_TO_SURFACE, "oppositeDirection" : true, "endBoundEntityFace" : qUnion([Q1]), "depth" : 25 * mm});
        }
        {
            var Q0;
            Q0=makeQuery(id+"F7.opExtrude","SWEPT_EDGE",EDGE,{"disambiguationData":[OSD([sQuery(id+"F6.wireOp",EDGE,"E19"),sQuery(id+"F6.wireOp",EDGE,"E21")])]});
            var Q1;
            Q1=makeQuery(id+"F7.opExtrude","SWEPT_EDGE",EDGE,{"disambiguationData":[OSD([sQuery(id+"F6.wireOp",EDGE,"E31"),sQuery(id+"F6.wireOp",EDGE,"E33")])]});
            fillet(context, id + "F12", {"entities" : qUnion([Q0, Q1]), "radius" : 1 * mm, "tangentPropagation" : true, "allowEdgeOverflow" : false});
        }
        {
            var Q0;
            Q0=makeQuery(id+"F7.opExtrude","SWEPT_EDGE",EDGE,{"disambiguationData":[OSD([sQuery(id+"F6.wireOp",EDGE,"E40"),sQuery(id+"F6.wireOp",EDGE,"E99")])]});
            var Q1;
            Q1=makeQuery(id+"F7.opExtrude","SWEPT_EDGE",EDGE,{"disambiguationData":[OSD([sQuery(id+"F6.wireOp",EDGE,"E47"),sQuery(id+"F6.wireOp",EDGE,"E54")])]});
            var Q2;
            Q2=makeQuery(id+"F7.opExtrude","SWEPT_EDGE",EDGE,{"disambiguationData":[OSD([sQuery(id+"F6.wireOp",EDGE,"E73"),sQuery(id+"F6.wireOp",EDGE,"E83")])]});
            var Q3;
            Q3=makeQuery(id+"F7.opExtrude","SWEPT_EDGE",EDGE,{"disambiguationData":[OSD([sQuery(id+"F6.wireOp",EDGE,"E82"),sQuery(id+"F6.wireOp",EDGE,"E83")])]});
            var Q4;
            Q4=makeQuery(id+"F7.opExtrude","SWEPT_EDGE",EDGE,{"disambiguationData":[OSD([sQuery(id+"F6.wireOp",EDGE,"E37"),sQuery(id+"F6.wireOp",EDGE,"E62")])]});
            fillet(context, id + "F13", {"entities" : qUnion([Q0, Q1, Q2, Q3, Q4]), "radius" : .5 * mm, "tangentPropagation" : true, "allowEdgeOverflow" : false});
        }
        {
            var Q0;
            Q0=makeQuery(id+"F7.opExtrude","CAP_FACE",FACE,{"disambiguationData":[OSD([sQuery(id+"F6.wireOp",EDGE,"E1.0"),sQuery(id+"F6.wireOp",EDGE,"E2.0")])],"isStart":false});
            cPlane(context, id + "F14", {"entities" : qUnion([Q0]), "cplaneType" : CPlaneType.OFFSET, "offset" : .6 * mm, "width" : 150 * mm, "height" : 150 * mm});
        }
        {
            var Q0;
            Q0=qCreatedBy(id+"F14.planeOp",FACE);
            var sketch = newSketch(context, id + "F15", { "sketchPlane" : qUnion([Q0])});
            skCircle(sketch, "E141.0", {"center": v(0, 0) * mm, "radius": 75 * mm, "construction": true});
            skCircle(sketch, "E142.0", {"center": v(0, 0) * mm, "radius": 77.6 * mm});
            skSolve(sketch);
        }
        {
            var Q0;
            Q0 = qSketchRegion(id + "F15", true);
            extrude(context, id + "F16", {"entities" : qUnion([Q0]), "depth" : (getVariable(context, 'WallThick')) * mm});
        }
        {
            var Q0;
            Q0=makeQuery(id+"F16.opExtrude","CAP_FACE",FACE,{"disambiguationData":[OSD([sQuery(id+"F15.wireOp",EDGE,"E142.0")])],"isStart":true});
            var sketch = newSketch(context, id + "F17", { "sketchPlane" : qUnion([Q0])});
            skCircle(sketch, "E143.0", {"center": v(0, 0) * mm, "radius": 77.6 * mm});
            skCircle(sketch, "E144.0", {"center": v(0, 0) * mm, "radius": 75.6 * mm});
            skSolve(sketch);
        }
        {
            var Q0;
            Q0 = qSketchRegion(id + "F17", true);
            extrude(context, id + "F18", {"entities" : qUnion([Q0]), "operationType" : NewBodyOperationType.ADD, "depth" : (getVariable(context, 'WallHeight') + getVariable(context, 'WallThick')) * mm});
        }
        {
            var Q0;
            Q0=makeQuery(id+"F7.opExtrude","CAP_VERTEX",VERTEX,{"disambiguationData":[OSD([sQuery(id+"F6.wireOp",EDGE,"E84"),sQuery(id+"F6.wireOp",EDGE,"E86")])],"isStart":true});
            var Q1;
            Q1=makeQuery(id+"F7.opExtrude","CAP_VERTEX",VERTEX,{"disambiguationData":[OSD([sQuery(id+"F6.wireOp",EDGE,"E84"),sQuery(id+"F6.wireOp",EDGE,"E86")])],"isStart":false});
            var Q2;
            Q2=makeQuery(id+"F7.opExtrude","CAP_VERTEX",VERTEX,{"disambiguationData":[OSD([sQuery(id+"F6.wireOp",EDGE,"E84"),sQuery(id+"F6.wireOp",EDGE,"E85")])],"isStart":false});
            cPlane(context, id + "F19", {"entities" : qUnion([Q0, Q1, Q2]), "cplaneType" : CPlaneType.THREE_POINT, "offset" : 25 * mm, "width" : 150 * mm, "height" : 150 * mm});
        }
        {
            var Q0;
            Q0=qCreatedBy(id+"F19.planeOp",FACE);
            var sketch = newSketch(context, id + "F20", { "sketchPlane" : qUnion([Q0])});
            skPoint(sketch, "E145.0", {"position": v(-8.21, 2) * mm});
            skPoint(sketch, "E146.0", {"position": v(8.21, 16) * mm});
            skPoint(sketch, "E147.0", {"position": v(8.21, 2) * mm});
            skPoint(sketch, "E148.0", {"position": v(-8.21, 16) * mm});
            skLineSegment(sketch, "E149", {"start": v(8.21, 2) * mm, "end": v(-8.21, 16) * mm, "construction": true});
            skText(sketch, "E150", { "text": "3E8", "fontName": "OpenSans-Regular.ttf"});
            skPoint(sketch, "E151", {"position": v(0, 9) * mm});
            const initialGuessF20  = {"E150": [-0.00452, 0.0055, 1, 0, 0.0038]};
            skSetInitialGuess(sketch, initialGuessF20);
            skSolve(sketch);
        }
        {
            var Q0;
            Q0 = qSketchRegion(id + "F20", true);
            var Q1;
            Q1=makeQuery(id+"F7.opExtrude","SWEPT_FACE",FACE,{"disambiguationData":[OSD([sQuery(id+"F6.wireOp",EDGE,"E84")])]});
            extrude(context, id + "F21", {"entities" : qUnion([Q0]), "operationType" : NewBodyOperationType.REMOVE, "oppositeDirection" : true, "endBoundEntityFace" : qUnion([Q1]), "depth" : (getVariable(context, 'WallThick') / 3.5) * mm});
        }
    });
